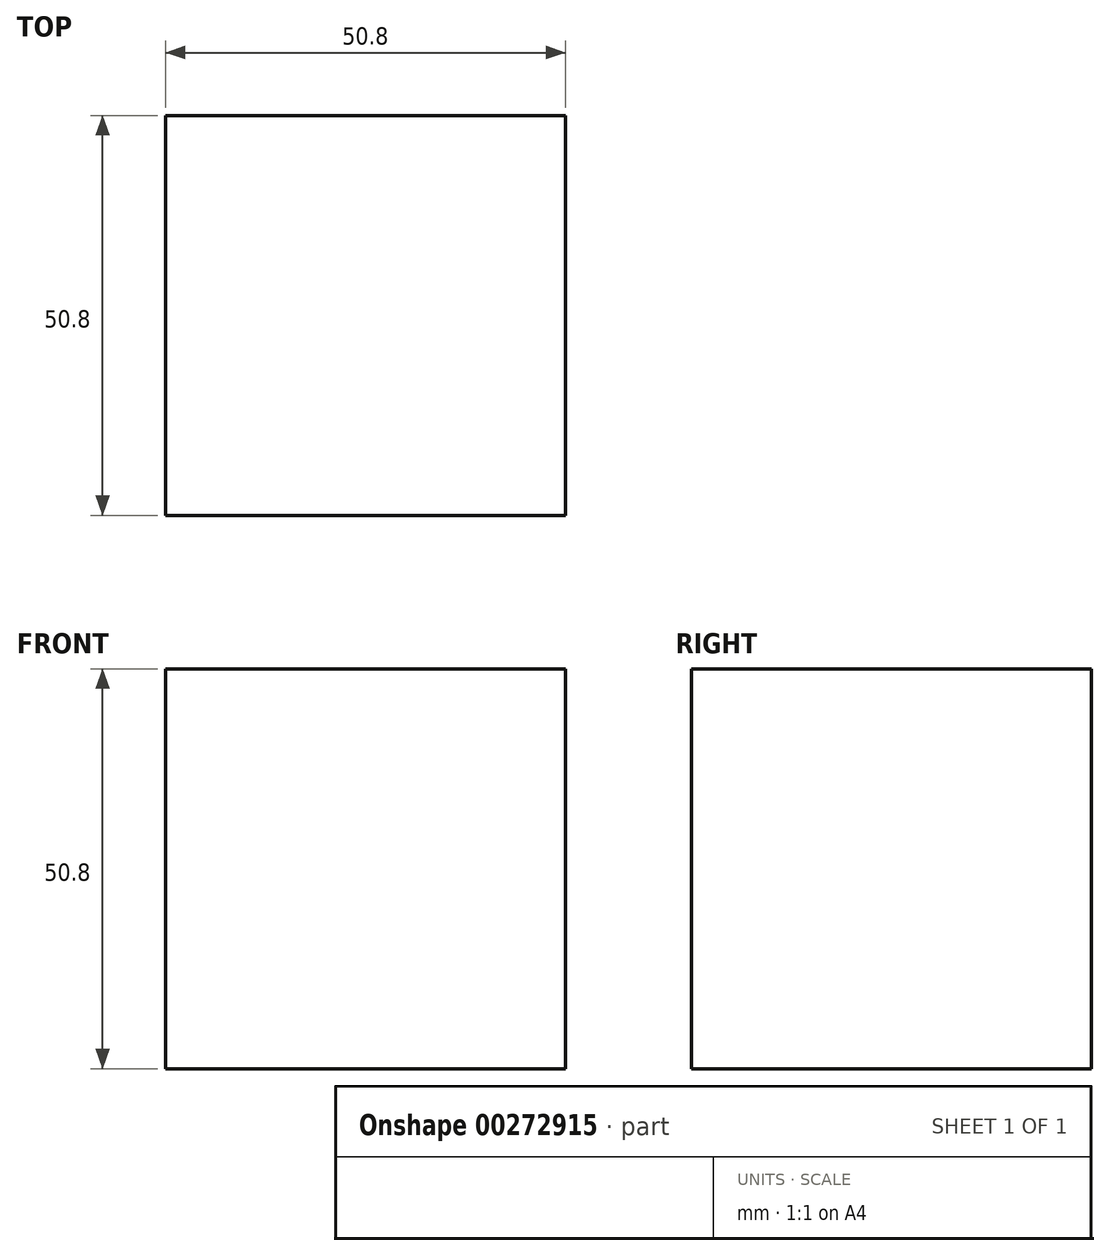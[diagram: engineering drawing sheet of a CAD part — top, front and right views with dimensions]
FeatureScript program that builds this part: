
annotation { "Feature Type Name" : "Feature", "Feature Type Description" : "" }
export const myFeature = defineFeature(function(context is Context, id is Id, definition is map)
    precondition{}
    {
        {
            var Q0;
            Q0=qCreatedBy(makeId("Front.planeOp"),FACE);
            var sketch = newSketch(context, id + "F0", { "sketchPlane" : qUnion([Q0])});
            skLineSegment(sketch, "E0.bottom", {"start": v(0, 0) * mm, "end": v(-50.8, 0) * mm});
            skLineSegment(sketch, "E0.top", {"start": v(0, 50.8) * mm, "end": v(-50.8, 50.8) * mm});
            skLineSegment(sketch, "E0.left", {"start": v(0, 0) * mm, "end": v(0, 50.8) * mm});
            skLineSegment(sketch, "E0.right", {"start": v(-50.8, 0) * mm, "end": v(-50.8, 50.8) * mm});
            skSolve(sketch);
        }
        {
            var Q0;
            Q0 = qSketchRegion(id + "F0", true);
            extrude(context, id + "F1", {"entities" : qUnion([Q0]), "depth" : 50.8 * mm});
        }
        {
            var Q0;
            Q0=makeQuery(id+"F1.opExtrude","CAP_FACE",FACE,{"disambiguationData":[OSD([sQuery(id+"F0.wireOp",EDGE,"E0.bottom"),sQuery(id+"F0.wireOp",EDGE,"E0.top"),sQuery(id+"F0.wireOp",EDGE,"E0.left"),sQuery(id+"F0.wireOp",EDGE,"E0.right")])],"isStart":false});
            var sketch = newSketch(context, id + "F2", { "sketchPlane" : qUnion([Q0])});
            skCircle(sketch, "E1", {"center": v(-26.76, 24.03) * mm, "radius": 15.34 * mm});
            skSolve(sketch);
        }
        {
            var Q0;
            Q0 = qSketchRegion(id + "F2", true);
            extrude(context, id + "F3", {"entities" : qUnion([Q0]), "operationType" : NewBodyOperationType.REMOVE, "depth" : 50.8 * mm});
        }
    });
